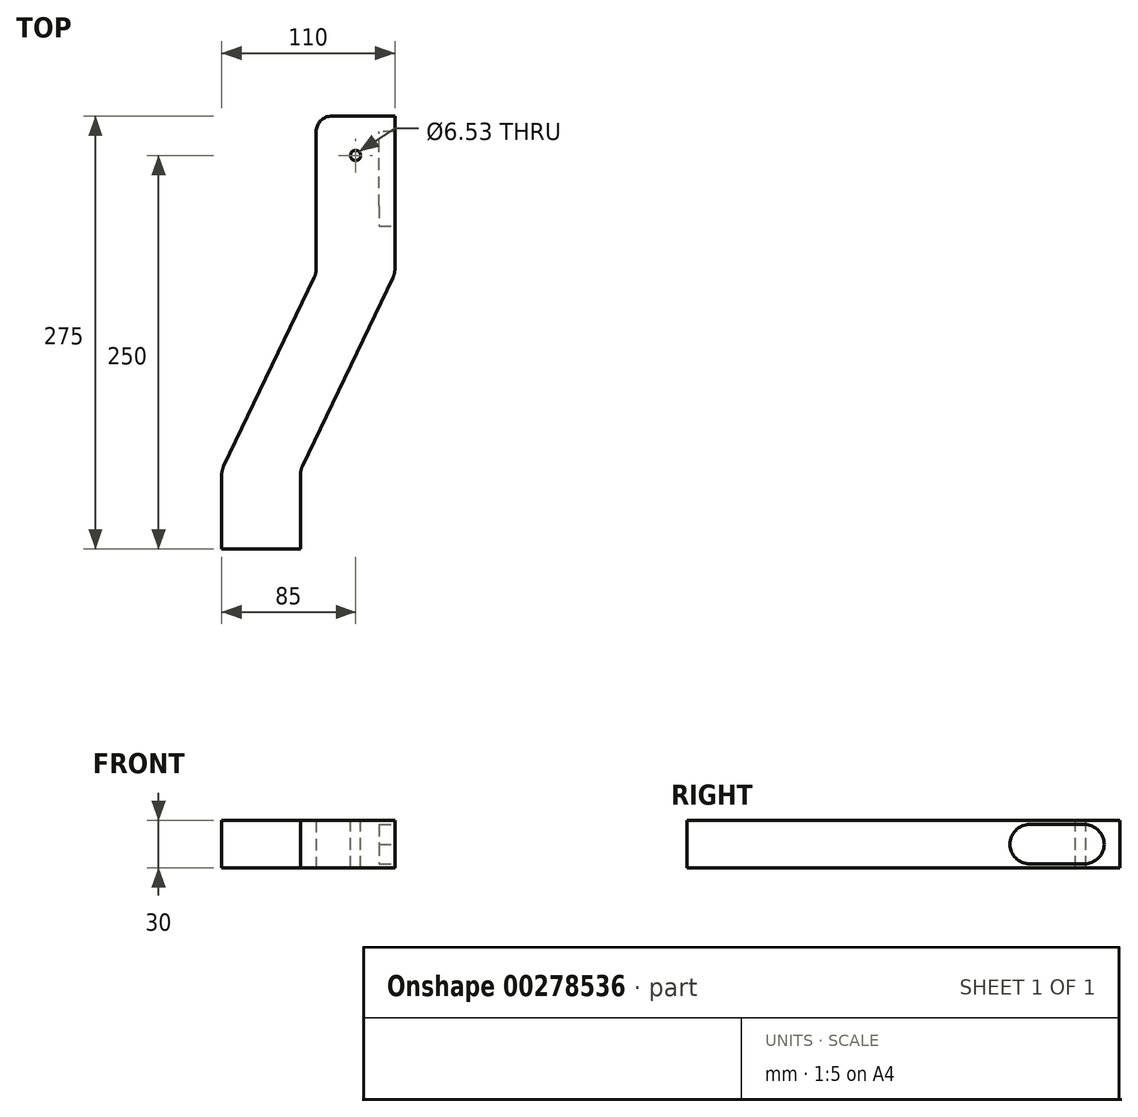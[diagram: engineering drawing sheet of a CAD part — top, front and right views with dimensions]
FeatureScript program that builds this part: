
annotation { "Feature Type Name" : "Feature", "Feature Type Description" : "" }
export const myFeature = defineFeature(function(context is Context, id is Id, definition is map)
    precondition{}
    {
        {
            var Q0;
            Q0=qCreatedBy(makeId("Top.planeOp"),FACE);
            var sketch = newSketch(context, id + "F0", { "sketchPlane" : qUnion([Q0])});
            skLineSegment(sketch, "E0.top", {"start": v(-25, -150) * mm, "end": v(25, -150) * mm});
            skPoint(sketch, "E0.middle", {"position": v(0, 0) * mm});
            skPoint(sketch, "E0.bottom.start.orphan", {"position": v(-25, 150) * mm});
            skLineSegment(sketch, "E1", {"start": v(-25, -150) * mm, "end": v(-25, -100) * mm});
            skLineSegment(sketch, "E2", {"start": v(-25, -100) * mm, "end": v(35, 25) * mm});
            skLineSegment(sketch, "E3", {"start": v(35, 25) * mm, "end": v(35, 125) * mm});
            skLineSegment(sketch, "E4", {"start": v(25, -150) * mm, "end": v(25, -100) * mm});
            skLineSegment(sketch, "E5", {"start": v(25, -100) * mm, "end": v(85, 25) * mm});
            skLineSegment(sketch, "E6", {"start": v(85, 25) * mm, "end": v(85, 125) * mm});
            skLineSegment(sketch, "E7", {"start": v(35, 125) * mm, "end": v(85, 125) * mm});
            skSolve(sketch);
        }
        {
            var Q0;
            Q0=qSketchRegion(id+"F0",true);
            extrude(context, id + "F1", {"entities" : qUnion([Q0]), "depth" : 30 * mm});
        }
        {
            var Q0;
            Q0=makeQuery(id+"F1.opExtrude","SWEPT_FACE",FACE,{"disambiguationData":[OSD([sQuery(id+"F0.wireOp",EDGE,"E6")])]});
            var sketch = newSketch(context, id + "F2", { "sketchPlane" : qUnion([Q0])});
            skLineSegment(sketch, "E8.bottom", {"start": v(55, 2.5) * mm, "end": v(115, 2.5) * mm});
            skLineSegment(sketch, "E8.top", {"start": v(55, 27.5) * mm, "end": v(115, 27.5) * mm});
            skLineSegment(sketch, "E8.left", {"start": v(55, 2.5) * mm, "end": v(55, 27.5) * mm});
            skLineSegment(sketch, "E8.right", {"start": v(115, 2.5) * mm, "end": v(115, 27.5) * mm});
            skPoint(sketch, "E8.middle", {"position": v(85, 15) * mm});
            skLineSegment(sketch, "E9", {"start": v(125, 15) * mm, "end": v(25, 15) * mm, "construction": true});
            skSolve(sketch);
        }
        {
            var Q0;
            Q0 = qSketchRegion(id + "F2", true);
            extrude(context, id + "F3", {"entities" : qUnion([Q0]), "operationType" : NewBodyOperationType.REMOVE, "oppositeDirection" : true, "depth" : 10 * mm});
        }
        {
            var Q0;
            Q0=makeQuery(id+"F1.opExtrude","SWEPT_EDGE",EDGE,{"disambiguationData":[OSD([sQuery(id+"F0.wireOp",EDGE,"E3"),sQuery(id+"F0.wireOp",EDGE,"E7")])]});
            fillet(context, id + "F4", {"entities" : qUnion([Q0]), "radius" : 10 * mm, "tangentPropagation" : true, "allowEdgeOverflow" : false});
        }
        {
            var Q0;
            Q0=makeQuery(id+"F1.opExtrude","CAP_FACE",FACE,{"disambiguationData":[OSD([sQuery(id+"F0.wireOp",EDGE,"E0.top"),sQuery(id+"F0.wireOp",EDGE,"E1"),sQuery(id+"F0.wireOp",EDGE,"E2"),sQuery(id+"F0.wireOp",EDGE,"E3"),sQuery(id+"F0.wireOp",EDGE,"E4"),sQuery(id+"F0.wireOp",EDGE,"E5"),sQuery(id+"F0.wireOp",EDGE,"E6"),sQuery(id+"F0.wireOp",EDGE,"E7")])],"isStart":false});
            var sketch = newSketch(context, id + "F5", { "sketchPlane" : qUnion([Q0])});
            skCircle(sketch, "E10", {"center": v(60, 100) * mm, "radius": 3.26 * mm});
            skLineSegment(sketch, "E11", {"start": v(85, 25) * mm, "end": v(35, 25) * mm, "construction": true});
            skLineSegment(sketch, "E12", {"start": v(60, 25) * mm, "end": v(60, 125) * mm, "construction": true});
            skSolve(sketch);
        }
        {
            var Q0;
            Q0 = qSketchRegion(id + "F5", true);
            extrude(context, id + "F6", {"entities" : qUnion([Q0]), "operationType" : NewBodyOperationType.REMOVE, "endBound" : BoundingType.THROUGH_ALL, "oppositeDirection" : true, "depth" : 25 * mm});
        }
        {
            var Q0;
            Q0=makeQuery(id+"F1.opExtrude","SWEPT_EDGE",EDGE,{"disambiguationData":[OSD([sQuery(id+"F0.wireOp",EDGE,"E4"),sQuery(id+"F0.wireOp",EDGE,"E5")])]});
            var Q1;
            Q1=makeQuery(id+"F1.opExtrude","SWEPT_EDGE",EDGE,{"disambiguationData":[OSD([sQuery(id+"F0.wireOp",EDGE,"E5"),sQuery(id+"F0.wireOp",EDGE,"E6")])]});
            var Q2;
            Q2=makeQuery(id+"F1.opExtrude","SWEPT_EDGE",EDGE,{"disambiguationData":[OSD([sQuery(id+"F0.wireOp",EDGE,"E1"),sQuery(id+"F0.wireOp",EDGE,"E2")])]});
            var Q3;
            Q3=makeQuery(id+"F1.opExtrude","SWEPT_EDGE",EDGE,{"disambiguationData":[OSD([sQuery(id+"F0.wireOp",EDGE,"E2"),sQuery(id+"F0.wireOp",EDGE,"E3")])]});
            var Q4;
            Q4=makeQuery(id+"F3.boolean.opBoolean","COPY",EDGE,{"derivedFrom":makeQuery(id+"F3.opExtrude","SWEPT_EDGE",EDGE,{"disambiguationData":[OSD([sQuery(id+"F2.wireOp",EDGE,"E8.top"),sQuery(id+"F2.wireOp",EDGE,"E8.right")])]})});
            var Q5;
            Q5=makeQuery(id+"F3.boolean.opBoolean","COPY",EDGE,{"derivedFrom":makeQuery(id+"F3.opExtrude","SWEPT_EDGE",EDGE,{"disambiguationData":[OSD([sQuery(id+"F2.wireOp",EDGE,"E8.bottom"),sQuery(id+"F2.wireOp",EDGE,"E8.right")])]})});
            var Q6;
            Q6=makeQuery(id+"F3.boolean.opBoolean","COPY",EDGE,{"derivedFrom":makeQuery(id+"F3.opExtrude","SWEPT_EDGE",EDGE,{"disambiguationData":[OSD([sQuery(id+"F2.wireOp",EDGE,"E8.top"),sQuery(id+"F2.wireOp",EDGE,"E8.left")])]})});
            var Q7;
            Q7=makeQuery(id+"F3.boolean.opBoolean","COPY",EDGE,{"derivedFrom":makeQuery(id+"F3.opExtrude","SWEPT_EDGE",EDGE,{"disambiguationData":[OSD([sQuery(id+"F2.wireOp",EDGE,"E8.bottom"),sQuery(id+"F2.wireOp",EDGE,"E8.left")])]})});
            fillet(context, id + "F7", {"entities" : qUnion([Q0, Q1, Q2, Q3, Q4, Q5, Q6, Q7]), "radius" : 12.7 * mm, "tangentPropagation" : true, "allowEdgeOverflow" : false});
        }
    });
